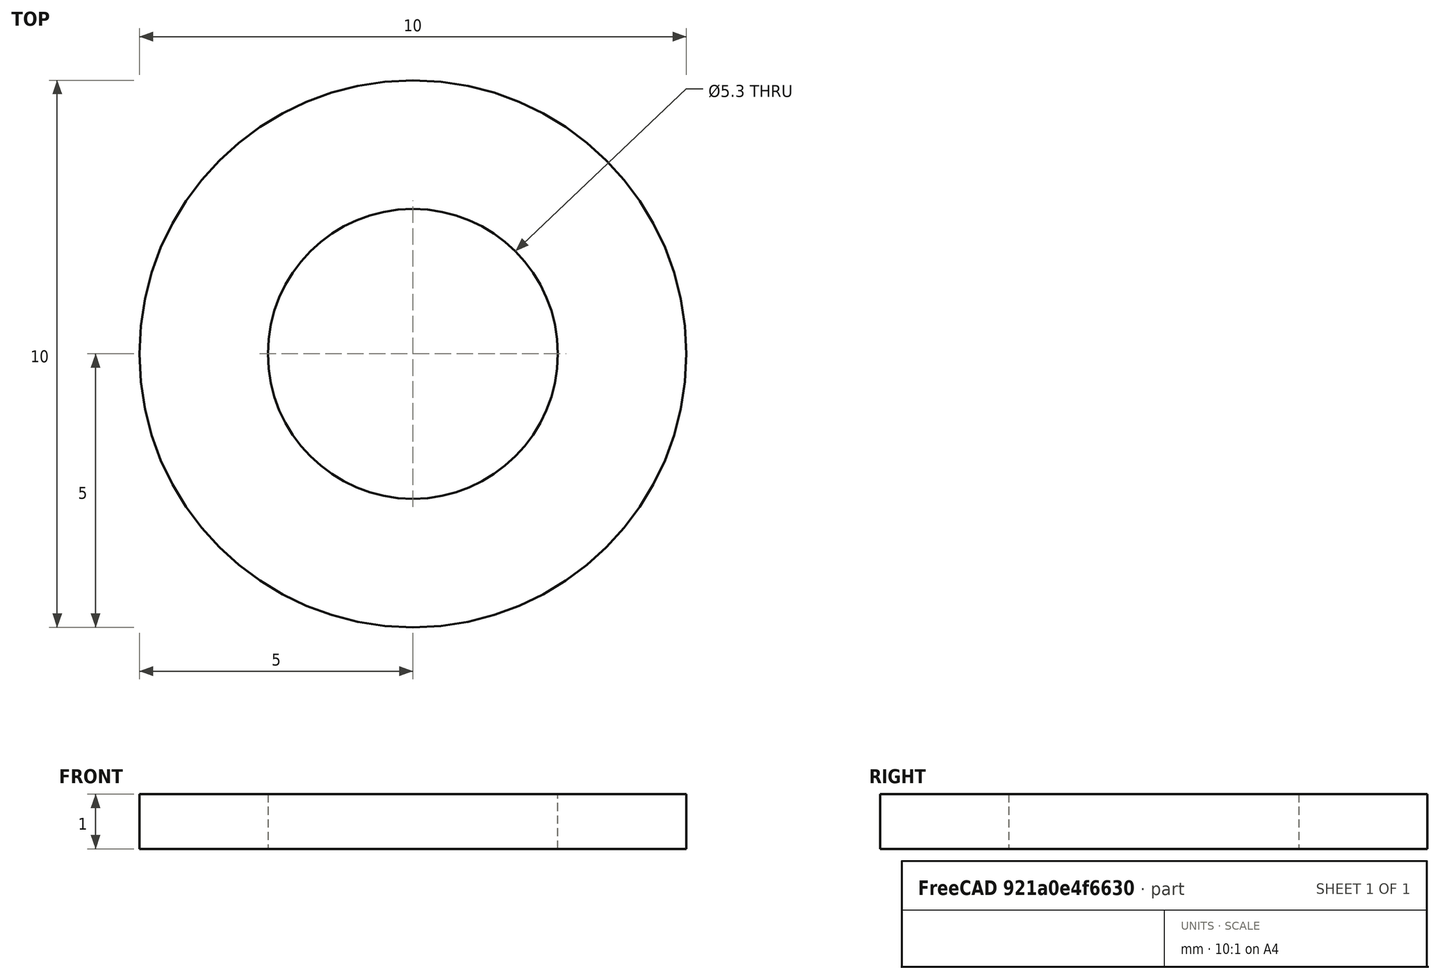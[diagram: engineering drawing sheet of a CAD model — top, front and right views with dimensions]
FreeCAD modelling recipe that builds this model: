
FCSTD DOCUMENT  (FreeCAD 1.0R39319 (Git))
Label: rondelleM5
License: All rights reserved
LicenseURL: https://en.wikipedia.org/wiki/All_rights_reserved
objects: Sketcher::SketchObject×1, PartDesign::Pad×1, PartDesign::Body×1
note: 6 computed .brp shape members not serialized (recipe doc carries the construction recipe); baked Part::Feature solids carry a one-line shape summary decoded from their .brp

FEATURE [Sketcher::SketchObject] Sketch
  ArcFitTolerance = 1e-06
  AttachmentSupport = -> [XY_Plane]
  FullyConstrained = true
  MakeInternals = false
  MapMode = 5
  sketch-geometry (2):
    g0: Circle CenterX=0 CenterY=0 CenterZ=0 NormalX=0 NormalY=0 NormalZ=1 AngleXU=0 Radius=2.65
    g1: Circle CenterX=0 CenterY=0 CenterZ=0 NormalX=0 NormalY=0 NormalZ=1 AngleXU=0 Radius=5
  constraints (4):
    c: Coincident(g0,g-1)
    c: Coincident(g1,g0)
    c: Diameter(g0) = 5.3
    c: Diameter(g1) = 10
FEATURE [PartDesign::Pad] Pad
  Direction = (0,0,1)
  Length = 1
  Length2 = 10
  Profile = -> Sketch
  ReferenceAxis = -> Sketch [N_Axis]
  Refine = true
  Suppressed = false
  Type = 0
FEATURE [PartDesign::Body] Body  label="Corps"
  AllowCompound = false
  Group = -> [Sketch,Pad]
  Origin = -> Origin
  Tip = -> Pad
